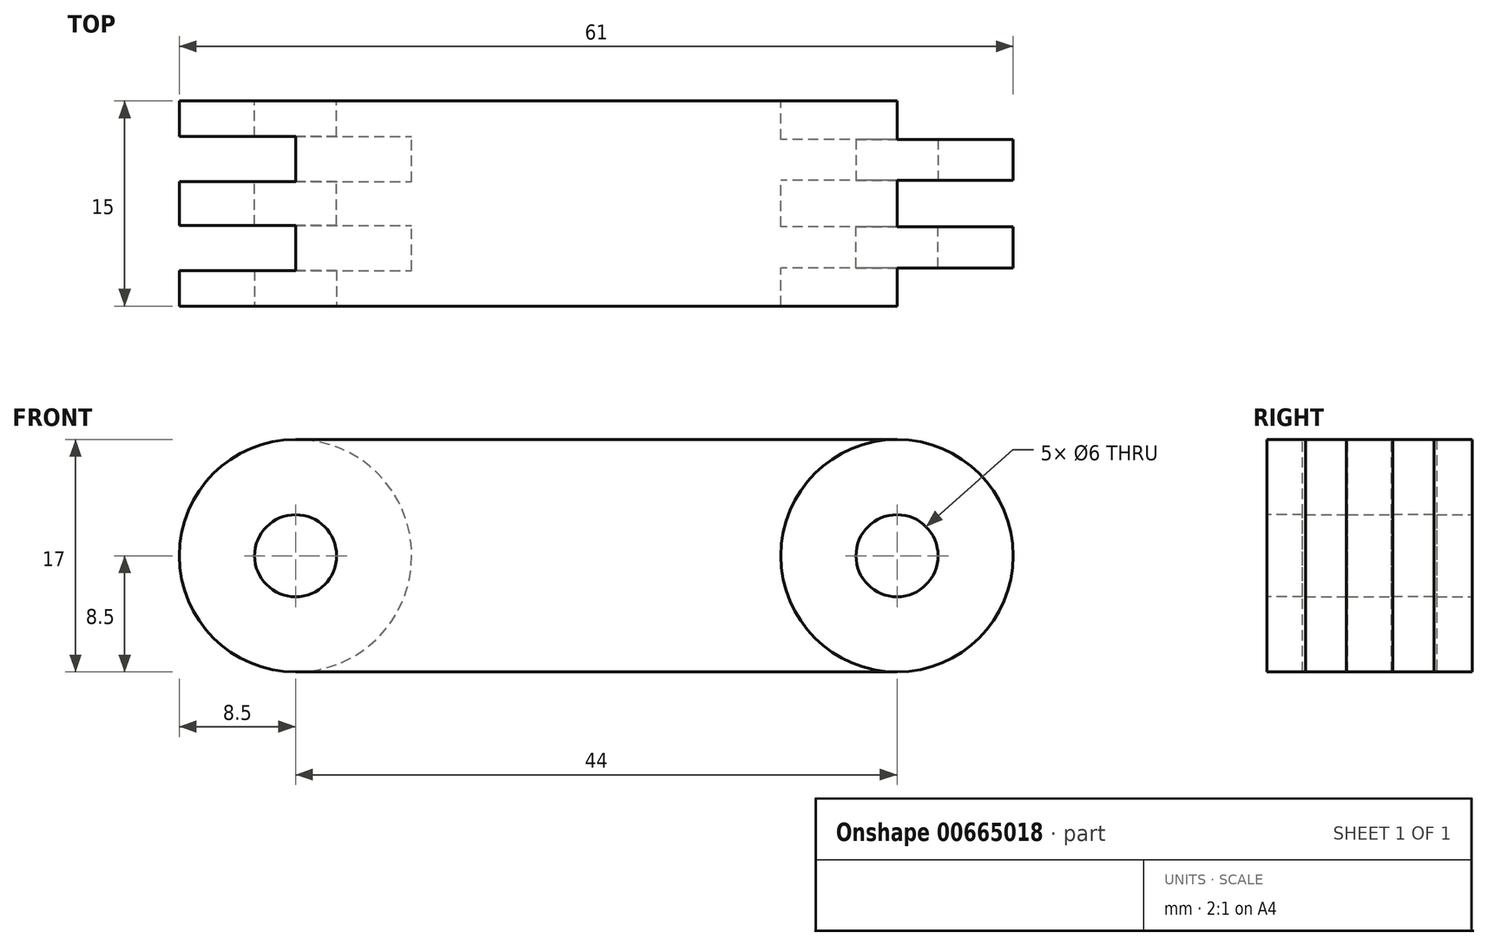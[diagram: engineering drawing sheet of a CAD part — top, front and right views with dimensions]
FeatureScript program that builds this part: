
annotation { "Feature Type Name" : "Feature", "Feature Type Description" : "" }
export const myFeature = defineFeature(function(context is Context, id is Id, definition is map)
    precondition{}
    {
        {
            var Q0;
            Q0=qCreatedBy(makeId("Front.planeOp"),FACE);
            var sketch = newSketch(context, id + "F0", { "sketchPlane" : qUnion([Q0])});
            skLineSegment(sketch, "E0.bottom", {"start": v(0, 0) * mm, "end": v(44, 0) * mm});
            skLineSegment(sketch, "E0.top", {"start": v(0, 17) * mm, "end": v(44, 17) * mm});
            skLineSegment(sketch, "E0.left", {"start": v(0, 0) * mm, "end": v(0, 17) * mm});
            skLineSegment(sketch, "E0.right", {"start": v(44, 0) * mm, "end": v(44, 17) * mm});
            skCircle(sketch, "E1", {"center": v(44, 8.5) * mm, "radius": 8.5 * mm});
            skCircle(sketch, "E2", {"center": v(0, 8.5) * mm, "radius": 8.5 * mm});
            skLineSegment(sketch, "E3", {"start": v(44, 8.5) * mm, "end": v(0, 8.5) * mm, "construction": true});
            skCircle(sketch, "E4", {"center": v(0, 8.5) * mm, "radius": 3 * mm});
            skCircle(sketch, "E5", {"center": v(44, 8.5) * mm, "radius": 3 * mm});
            skSolve(sketch);
        }
        {
            var Q0;
            {var subQ0=sQuery(id+"F0.wireOp",EDGE,"E0.bottom");Q0=makeQuery(id+"F0.imprint","IMPRINT",FACE,{"disambiguationData":[TD([[makeQuery(id+"F0.imprint","IMPRINT",EDGE,{"derivedFrom":subQ0}),1.0]])]});}
            extrude(context, id + "F1", {"entities" : qUnion([Q0]), "endBound" : BoundingType.SYMMETRIC, "depth" : 15 * mm, "offsetDistance" : 25 * mm});
        }
        {
            var Q0;
            {var subQ1=sQuery(id+"F0.wireOp",EDGE,"E0.left");var subQ3=sQuery(id+"F0.wireOp",EDGE,"E4");var subQ4=makeQuery(id+"F0.imprint","INTERSECT",VERTEX,{"disambiguationData":[OD(0.0)],"derivedFrom":[subQ1,subQ3]});Q0=makeQuery(id+"F0.imprint","IMPRINT",FACE,{"disambiguationData":[TD([[makeQuery(id+"F0.imprint","IMPRINT",EDGE,{"disambiguationData":[TD([[subQ4,-1.0]])],"derivedFrom":subQ3}),-1.0]])]});}
            var Q1;
            {var subQ1=sQuery(id+"F0.wireOp",EDGE,"E0.left");var subQ3=sQuery(id+"F0.wireOp",EDGE,"E4");var subQ4=makeQuery(id+"F0.imprint","INTERSECT",VERTEX,{"disambiguationData":[OD(0.0)],"derivedFrom":[subQ1,subQ3]});Q1=makeQuery(id+"F0.imprint","IMPRINT",FACE,{"disambiguationData":[TD([[makeQuery(id+"F0.imprint","IMPRINT",EDGE,{"disambiguationData":[TD([[subQ4,1.0]])],"derivedFrom":subQ3}),-1.0]])]});}
            extrude(context, id + "F2", {"entities" : qUnion([Q0, Q1]), "operationType" : NewBodyOperationType.ADD, "endBound" : BoundingType.SYMMETRIC, "depth" : 3.2 * mm, "offsetDistance" : 25 * mm});
        }
        {
            var Q0;
            Q0=makeQuery(id+"F1.opExtrude","CAP_FACE",FACE,{"disambiguationData":[OSD([sQuery(id+"F0.wireOp",EDGE,"E0.bottom"),sQuery(id+"F0.wireOp",EDGE,"E0.top"),sQuery(id+"F0.wireOp",EDGE,"E1"),sQuery(id+"F0.wireOp",EDGE,"E2")])],"isStart":true});
            var sketch = newSketch(context, id + "F3", { "sketchPlane" : qUnion([Q0])});
            skArc(sketch, "E6.0.0", {"start": v(0, 0) * mm, "mid": v(8.5, 8.5) * mm, "end": v(0, 17) * mm});
            skArc(sketch, "E6.0.1", {"start": v(0, 17) * mm, "mid": v(-8.5, 8.5) * mm, "end": v(0, 0) * mm});
            skCircle(sketch, "E7", {"center": v(0, 8.5) * mm, "radius": 3 * mm});
            skCircle(sketch, "E8", {"center": v(0, 8.5) * mm, "radius": 8.5 * mm});
            skSolve(sketch);
        }
        {
            var Q0;
            Q0=makeQuery(id+"F3.imprint","IMPRINT",FACE,{"disambiguationData":[TD([[makeQuery(id+"F3.imprint","IMPRINT",EDGE,{"derivedFrom":sQuery(id+"F3.wireOp",EDGE,"E7")}),-1.0]])]});
            extrude(context, id + "F4", {"entities" : qUnion([Q0]), "operationType" : NewBodyOperationType.ADD, "oppositeDirection" : true, "depth" : 2.6 * mm, "offsetDistance" : 25 * mm});
        }
        {
            var Q0;
            Q0=makeQuery(id+"F1.opExtrude","CAP_FACE",FACE,{"disambiguationData":[OSD([sQuery(id+"F0.wireOp",EDGE,"E0.bottom"),sQuery(id+"F0.wireOp",EDGE,"E0.top"),sQuery(id+"F0.wireOp",EDGE,"E1"),sQuery(id+"F0.wireOp",EDGE,"E2")])],"isStart":false});
            var sketch = newSketch(context, id + "F5", { "sketchPlane" : qUnion([Q0])});
            skArc(sketch, "E9.0.0", {"start": v(0, 17) * mm, "mid": v(-8.5, 8.5) * mm, "end": v(0, 0) * mm});
            skArc(sketch, "E9.0.1", {"start": v(0, 0) * mm, "mid": v(8.5, 8.5) * mm, "end": v(0, 17) * mm});
            skCircle(sketch, "E10", {"center": v(0, 8.5) * mm, "radius": 3 * mm});
            skCircle(sketch, "E11", {"center": v(0, 8.5) * mm, "radius": 8.5 * mm});
            skSolve(sketch);
        }
        {
            var Q0;
            Q0=makeQuery(id+"F5.imprint","IMPRINT",FACE,{"disambiguationData":[TD([[makeQuery(id+"F5.imprint","IMPRINT",EDGE,{"derivedFrom":sQuery(id+"F5.wireOp",EDGE,"E10")}),-1.0]])]});
            extrude(context, id + "F6", {"entities" : qUnion([Q0]), "operationType" : NewBodyOperationType.ADD, "oppositeDirection" : true, "depth" : 2.6 * mm, "offsetDistance" : 25 * mm});
        }
        {
            var Q0;
            Q0=qCreatedBy(makeId("Front.planeOp"),FACE);
            cPlane(context, id + "F7", {"entities" : qUnion([Q0]), "cplaneType" : CPlaneType.OFFSET, "offset" : 3.4 / 2 * mm, "width" : 150 * mm, "height" : 150 * mm});
        }
        {
            var Q0;
            Q0=qCreatedBy(id+"F7.planeOp",FACE);
            var sketch = newSketch(context, id + "F8", { "sketchPlane" : qUnion([Q0])});
            skCircle(sketch, "E12.0", {"center": v(44, 8.5) * mm, "radius": 3 * mm});
            skCircle(sketch, "E13", {"center": v(44, 8.5) * mm, "radius": 8.5 * mm});
            skSolve(sketch);
        }
        {
            var Q0;
            Q0=makeQuery(id+"F8.imprint","IMPRINT",FACE,{"disambiguationData":[TD([[makeQuery(id+"F8.imprint","IMPRINT",EDGE,{"derivedFrom":sQuery(id+"F8.wireOp",EDGE,"E12.0")}),-1.0]])]});
            extrude(context, id + "F9", {"entities" : qUnion([Q0]), "operationType" : NewBodyOperationType.ADD, "depth" : 3 * mm, "offsetDistance" : 25 * mm});
        }
        {
            var Q0;
            Q0=qCreatedBy(makeId("Front.planeOp"),FACE);
            cPlane(context, id + "F10", {"entities" : qUnion([Q0]), "cplaneType" : CPlaneType.OFFSET, "offset" : (3.4 / 2) * mm, "oppositeDirection" : true, "width" : 150 * mm, "height" : 150 * mm});
        }
        {
            var Q0;
            Q0=qCreatedBy(id+"F10.planeOp",FACE);
            var sketch = newSketch(context, id + "F11", { "sketchPlane" : qUnion([Q0])});
            skCircle(sketch, "E14.0", {"center": v(44, 8.5) * mm, "radius": 3 * mm});
            skCircle(sketch, "E15", {"center": v(44, 8.5) * mm, "radius": 8.5 * mm});
            skSolve(sketch);
        }
        {
            var Q0;
            Q0=makeQuery(id+"F11.imprint","IMPRINT",FACE,{"disambiguationData":[TD([[makeQuery(id+"F11.imprint","IMPRINT",EDGE,{"derivedFrom":sQuery(id+"F11.wireOp",EDGE,"E14.0")}),-1.0]])]});
            extrude(context, id + "F12", {"entities" : qUnion([Q0]), "operationType" : NewBodyOperationType.ADD, "oppositeDirection" : true, "depth" : 3 * mm, "offsetDistance" : 25 * mm});
        }
    });
